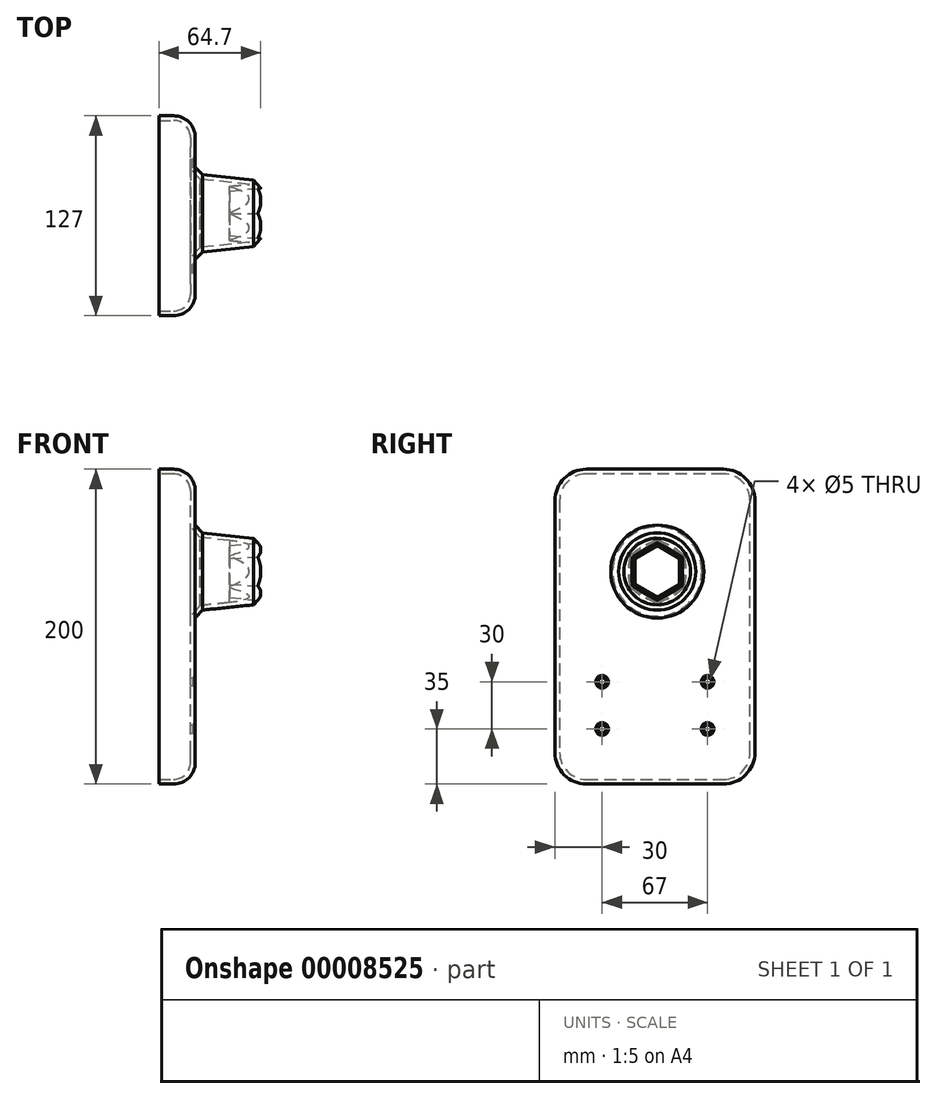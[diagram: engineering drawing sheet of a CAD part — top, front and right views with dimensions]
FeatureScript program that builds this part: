
annotation { "Feature Type Name" : "Feature", "Feature Type Description" : "" }
export const myFeature = defineFeature(function(context is Context, id is Id, definition is map)
    precondition{}
    {
        {
            var Q0;
            Q0=qCreatedBy(makeId("Right.planeOp"),FACE);
            var sketch = newSketch(context, id + "F0", { "sketchPlane" : qUnion([Q0])});
            skLineSegment(sketch, "E0", {"start": v(-127, -100) * mm, "end": v(0, -100) * mm});
            skLineSegment(sketch, "E1", {"start": v(0, -100) * mm, "end": v(0, 100) * mm});
            skLineSegment(sketch, "E2", {"start": v(0, 100) * mm, "end": v(-127, 100) * mm});
            skLineSegment(sketch, "E3", {"start": v(-127, 100) * mm, "end": v(-127, -100) * mm});
            skSolve(sketch);
        }
        {
            var Q0;
            Q0=makeQuery(id+"F0.imprint","IMPRINT",FACE,{"disambiguationData":[TD([[makeQuery(id+"F0.imprint","IMPRINT",EDGE,{"derivedFrom":sQuery(id+"F0.wireOp",EDGE,"E0")}),1.0]])]});
            extrude(context, id + "F1", {"entities" : qUnion([Q0]), "depth" : 23.1 * mm, "offsetDistance" : 25 * mm});
        }
        {
            var Q0;
            Q0=makeQuery(id+"F1.opExtrude","CAP_FACE",FACE,{"disambiguationData":[OSD([sQuery(id+"F0.wireOp",EDGE,"E0"),sQuery(id+"F0.wireOp",EDGE,"E1"),sQuery(id+"F0.wireOp",EDGE,"E2"),sQuery(id+"F0.wireOp",EDGE,"E3")])],"isStart":false});
            var sketch = newSketch(context, id + "F2", { "sketchPlane" : qUnion([Q0])});
            skCircle(sketch, "E4", {"center": v(-62, 35) * mm, "radius": 25 * mm});
            skSolve(sketch);
        }
        {
            var Q0;
            Q0 = qSketchRegion(id + "F2", true);
            extrude(context, id + "F3", {"entities" : qUnion([Q0]), "operationType" : NewBodyOperationType.ADD, "depth" : 41.6 * mm, "offsetDistance" : 25 * mm, "hasDraft" : true, "draftAngle" : 6 * degree, "draftPullDirection" : true});
        }
        {
            var Q0;
            Q0=makeQuery(id+"F1.opExtrude","SWEPT_EDGE",EDGE,{"disambiguationData":[OSD([sQuery(id+"F0.wireOp",EDGE,"E2"),sQuery(id+"F0.wireOp",EDGE,"E3")])]});
            var Q1;
            Q1=makeQuery(id+"F1.opExtrude","SWEPT_EDGE",EDGE,{"disambiguationData":[OSD([sQuery(id+"F0.wireOp",EDGE,"E1"),sQuery(id+"F0.wireOp",EDGE,"E2")])]});
            var Q2;
            Q2=makeQuery(id+"F1.opExtrude","SWEPT_EDGE",EDGE,{"disambiguationData":[OSD([sQuery(id+"F0.wireOp",EDGE,"E0"),sQuery(id+"F0.wireOp",EDGE,"E1")])]});
            var Q3;
            Q3=makeQuery(id+"F1.opExtrude","SWEPT_EDGE",EDGE,{"disambiguationData":[OSD([sQuery(id+"F0.wireOp",EDGE,"E0"),sQuery(id+"F0.wireOp",EDGE,"E3")])]});
            fillet(context, id + "F4", {"entities" : qUnion([Q0, Q1, Q2, Q3]), "radius" : 20 * mm, "tangentPropagation" : true, "allowEdgeOverflow" : false});
        }
        {
            var Q0;
            Q0=makeQuery(id+"F1.opExtrude","CAP_EDGE",EDGE,{"disambiguationData":[OSD([sQuery(id+"F0.wireOp",EDGE,"E0")])],"isStart":false});
            var Q1;
            Q1=makeQuery(id+"F3.opExtrude","CAP_EDGE",EDGE,{"disambiguationData":[OSD([sQuery(id+"F2.wireOp",EDGE,"E4")])],"isStart":true});
            fillet(context, id + "F5", {"entities" : qUnion([Q0, Q1]), "radius" : 13.8 * mm, "tangentPropagation" : true, "defaultsChanged" : true, "allowEdgeOverflow" : false, "vertexSettings" : []});
        }
        {
            var Q0;
            Q0=makeQuery(id+"F3.opExtrude","CAP_FACE",FACE,{"disambiguationData":[OSD([sQuery(id+"F2.wireOp",EDGE,"E4")])],"isStart":false});
            var sketch = newSketch(context, id + "F6", { "sketchPlane" : qUnion([Q0])});
            skCircle(sketch, "E5.cCircle", {"center": v(-62, 35) * mm, "radius": 16 * mm, "construction": true});
            skLineSegment(sketch, "E5.0", {"start": v(-46, 44.24) * mm, "end": v(-46, 25.76) * mm});
            skLineSegment(sketch, "E5.1", {"start": v(-46, 25.76) * mm, "end": v(-62, 16.52) * mm});
            skLineSegment(sketch, "E5.2", {"start": v(-62, 16.52) * mm, "end": v(-78, 25.76) * mm});
            skLineSegment(sketch, "E5.3", {"start": v(-78, 25.76) * mm, "end": v(-78, 44.24) * mm});
            skLineSegment(sketch, "E5.4", {"start": v(-78, 44.24) * mm, "end": v(-62, 53.48) * mm});
            skLineSegment(sketch, "E5.5", {"start": v(-62, 53.48) * mm, "end": v(-46, 44.24) * mm});
            skPoint(sketch, "E5.0.midPoint", {"position": v(-46, 35) * mm});
            skSolve(sketch);
        }
        {
            var Q0;
            Q0 = qSketchRegion(id + "F6", true);
            extrude(context, id + "F7", {"entities" : qUnion([Q0]), "operationType" : NewBodyOperationType.REMOVE, "oppositeDirection" : true, "depth" : 20 * mm, "hasDraft" : true, "draftAngle" : 5 * degree, "draftPullDirection" : true, "hasSecondDirectionDraft" : true, "secondDirectionDraftAngle" : 3 * degree});
        }
        {
            var Q0;
            Q0=makeQuery(id+"F3.opExtrude","SWEPT_FACE",FACE,{"disambiguationData":[OSD([sQuery(id+"F2.wireOp",EDGE,"E4")])]});
            chamfer(context, id + "F8", {"entities" : qUnion([Q0]), "width" : 5 * mm, "tangentPropagation" : true});
        }
        {
            var Q0;
            Q0=makeQuery(id+"F1.opExtrude","CAP_FACE",FACE,{"disambiguationData":[OSD([sQuery(id+"F0.wireOp",EDGE,"E0"),sQuery(id+"F0.wireOp",EDGE,"E1"),sQuery(id+"F0.wireOp",EDGE,"E2"),sQuery(id+"F0.wireOp",EDGE,"E3")])],"isStart":true});
            var Q1;
            Q1=makeQuery(id+"F7.boolean.opBoolean","COPY",FACE,{"derivedFrom":makeQuery(id+"F7.opExtrude","CAP_FACE",FACE,{"disambiguationData":[OSD([sQuery(id+"F6.wireOp",EDGE,"E5.0"),sQuery(id+"F6.wireOp",EDGE,"E5.1"),sQuery(id+"F6.wireOp",EDGE,"E5.2"),sQuery(id+"F6.wireOp",EDGE,"E5.3"),sQuery(id+"F6.wireOp",EDGE,"E5.4"),sQuery(id+"F6.wireOp",EDGE,"E5.5")])],"isStart":false})});
            shell(context, id + "F9", {"entities" : qUnion([Q0, Q1]), "thickness" : 3 * mm});
        }
        {
            var Q0;
            Q0=makeQuery(id+"F1.opExtrude","CAP_FACE",FACE,{"disambiguationData":[OSD([sQuery(id+"F0.wireOp",EDGE,"E0"),sQuery(id+"F0.wireOp",EDGE,"E1"),sQuery(id+"F0.wireOp",EDGE,"E2"),sQuery(id+"F0.wireOp",EDGE,"E3")])],"isStart":false});
            var sketch = newSketch(context, id + "F10", { "sketchPlane" : qUnion([Q0])});
            skPoint(sketch, "E6", {"position": v(-97, -35) * mm});
            skPoint(sketch, "E7", {"position": v(-30, -35) * mm});
            skPoint(sketch, "E8", {"position": v(-97, -65) * mm});
            skPoint(sketch, "E9", {"position": v(-30, -65) * mm});
            skSolve(sketch);
        }
        {
            var Q0;
            Q0=sQuery(id+"F10.wireOp",VERTEX,"E9");
            var Q1;
            Q1=sQuery(id+"F10.wireOp",VERTEX,"E8");
            var Q2;
            Q2=sQuery(id+"F10.wireOp",VERTEX,"E6");
            var Q3;
            Q3=sQuery(id+"F10.wireOp",VERTEX,"E7");
            var Q4;
            Q4=makeQuery(id+"F1.opExtrude","SWEPT_BODY",BODY,{"disambiguationData":[OSD([sQuery(id+"F0.wireOp",EDGE,"E0"),sQuery(id+"F0.wireOp",EDGE,"E1"),sQuery(id+"F0.wireOp",EDGE,"E2"),sQuery(id+"F0.wireOp",EDGE,"E3")])]});
            hole(context, id + "F11", {"style" : HoleStyle.C_SINK, "holeDiameter" : 5 * mm, "cSinkDiameter" : 8 * mm, "endStyle" : HoleEndStyle.THROUGH, "locations" : qUnion([Q0, Q1, Q2, Q3]), "scope" : qUnion([Q4]), "cSinkAngle" : 90 * degree, "majorDiameter" : 5 * mm, "tappedDepth" : 12 * mm, "tapClearance" : 3});
        }
    });
